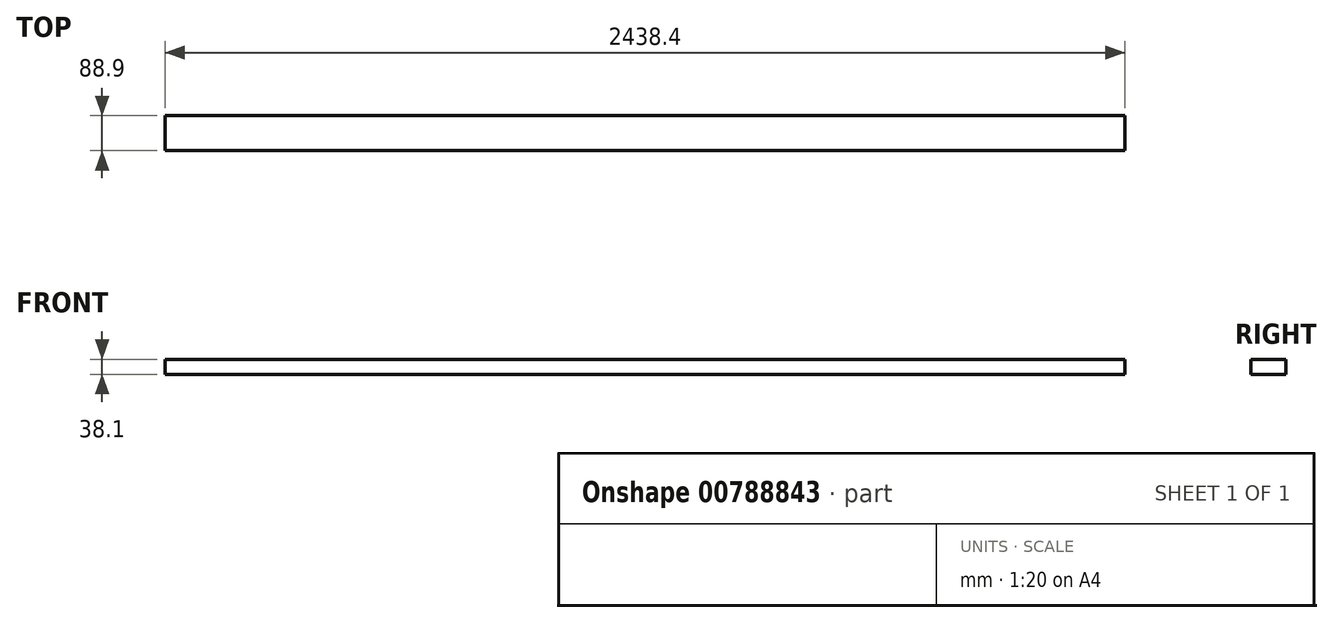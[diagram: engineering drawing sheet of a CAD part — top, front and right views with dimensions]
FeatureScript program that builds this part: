
annotation { "Feature Type Name" : "Feature", "Feature Type Description" : "" }
export const myFeature = defineFeature(function(context is Context, id is Id, definition is map)
    precondition{}
    {
        {
            var Q0;
            Q0=qCreatedBy(makeId("Front.planeOp"),FACE);
            var sketch = newSketch(context, id + "F0", { "sketchPlane" : qUnion([Q0])});
            skLineSegment(sketch, "E0.bottom", {"start": v(-318.71, 38.1) * mm, "end": v(2119.69, 38.1) * mm});
            skLineSegment(sketch, "E0.top", {"start": v(-318.71, 0) * mm, "end": v(2119.69, 0) * mm});
            skLineSegment(sketch, "E0.left", {"start": v(-318.71, 38.1) * mm, "end": v(-318.71, 0) * mm});
            skLineSegment(sketch, "E0.right", {"start": v(2119.69, 38.1) * mm, "end": v(2119.69, 0) * mm});
            skSolve(sketch);
        }
        {
            var Q0;
            Q0=makeQuery(id+"F0.imprint","IMPRINT",FACE,{"disambiguationData":[TD([[makeQuery(id+"F0.imprint","IMPRINT",EDGE,{"derivedFrom":sQuery(id+"F0.wireOp",EDGE,"E0.bottom")}),-1.0]])]});
            extrude(context, id + "F1", {"entities" : qUnion([Q0]), "depth" : 88.9 * mm, "offsetDistance" : 25.4 * mm});
        }
    });
